# Revit family: Hager-Orion_Plus-IP66-D250-Cl.II-Poly_encl-630A-NoHosted-BE-fr
name_source: partatom
category: Electrical Equipment
units: mm (PartAtom-declared; Revit-internal decimal feet)

## family parameters
Always vertical = Yes
Cut with Voids When Loaded = No
Panel Configuration = Two Columns, Circuits Across
Part Type = Panelboard
Room Calculation Point = No
Round Connector Dimension = Use Diameter
Shared = No
Work Plane-Based = Yes

## types (2) — shared parameters
Default Elevation = 1219 mm
EF000003 - mode de pose = EV000384 - saillie
EF000007 - couleur = EV000270 - gris
EF000008 - largeur = 500 mm  [stored 1.64042 ft]
EF000040 - hauteur = 650 mm  [stored 2.13255 ft]
EF000049 - profondeur = 250 mm  [stored 0.82021 ft]
EF000116 - numéro RAL = 7035
EF000118 - avec cadre/support de montage = No
EF000266 - nombre de rangées = 4
EF000339 - type de capot = EV004216 - porte
EF001088 - possibilité de montage en saillie = No
EF001131 - profondeur intérieure = 250 mm  [stored 0.82021 ft]
EF001596 - matériau du boîtier/corps = EV000139 - plastique
EF002950 - largeur en nombre de modules = 24
EF003532 - convient pour utilisation à l’extérieur = Yes
EF004427 - nombre de modules = 96
EF004464 - type de porte = EV002646 - unique
EF005474 - indice de protection (IP) = EV006422 - IP66
EF006306 - avec serrure = Yes
EF007800 - adapté à un parafoudre = No
EF008873 - courant nominal (In) = 630 A
EF009212 - finition du couvercle = EV000116 - fermé
EF015940 - couvercle avec décharge de pression = No
HG000002 - avec porte = Yes
HG000003 - Gamme = Orion Plus
HG000006 - Encastré = No
HG000009 - Porte à double battant = No
HG000010 - Portes asymétriques = No
HG000023 - Armoire double section = No
HG000024 - Hauteur de la section basse = 600 mm
HG000026 - Installation au sol = No
Manufacturer = Hager
Type Comments = Orion Plus
zero-valued in all types: EF000218 - profondeur d'encastrement, EF000437 - nombre d'entrées de conduit, EF009554 - nombre d'ouvertures pour plaques à bride, HG000027 - Hauteur du socle

## per-type parameters (varying)
| type | EF004293 - indice de protection contre les chocs (IK) | EF006244 - couvercle/porte transparent(e) | EF009170 - épaisseur de matériau du boîtier | EF009171 - épaisseur de matériau de la porte/du couvercle | HG000004 - Référence fabricant |
| saillie IP66 L500 H650 P250  - FL221B | EV008784 - IK10 | No | 2 mm  [stored 0.00656168 ft] | 2 mm  [stored 0.00656168 ft] | FL221B |
| saillie IP66 L500 H650 P250  - FL271B | EV006814 - IK08 | Yes | 3 mm  [stored 0.00984252 ft] | 3 mm  [stored 0.00984252 ft] | FL271B |

note: [stored X ft] marks values corroborated as IEEE doubles in the binary element streams (Revit-internal decimal feet)

## geometry (parser evidence)
native form markers: Blend x4, Sweep x5
no freeform markers — native parametric forms only
